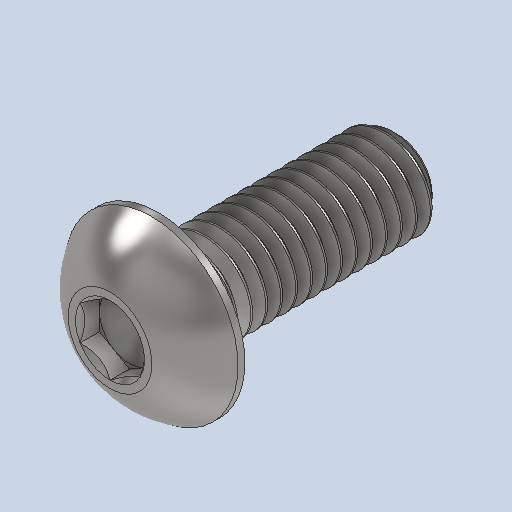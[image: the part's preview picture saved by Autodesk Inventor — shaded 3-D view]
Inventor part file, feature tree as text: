
AUTODESK INVENTOR PART (.ipt)
format: ipt  version: 2024 (Build 280153000, 153)  size: 598,016 bytes
history: native  units: in
note: dims shown in document units (in); Inventor stores cm internally (conversion verified against a paired STEP export)
features: revolve x1
ambient origin geometry x8: Origin, YZ Plane, XZ Plane, XY Plane, X Axis, Y Axis, Z Axis, Center Point
bodies: Solid1 (feature_tree)
feature tree (1):
  revolve  "Revolve2"  [1 undecoded]
note: 1 required parameter value undecoded (feature->parameter linkage not recoverable at this tier; creation-order binding heuristic only, values carry confidence <= 0.55)
